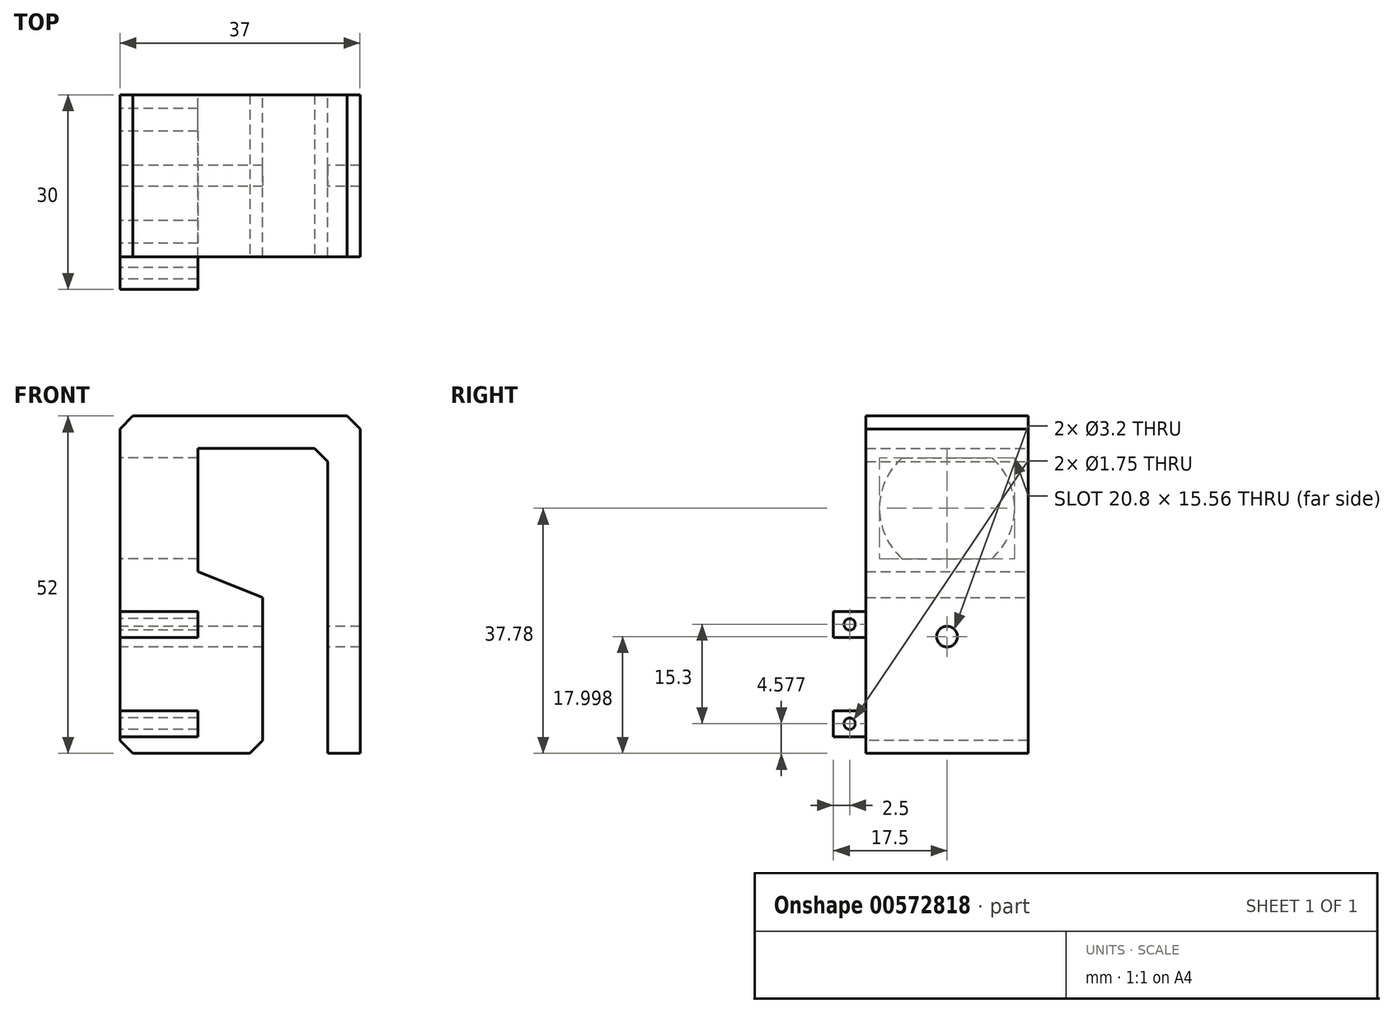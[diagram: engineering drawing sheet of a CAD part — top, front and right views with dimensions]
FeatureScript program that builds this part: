
annotation { "Feature Type Name" : "Feature", "Feature Type Description" : "" }
export const myFeature = defineFeature(function(context is Context, id is Id, definition is map)
    precondition{}
    {
        {
            var Q0;
            Q0=qCreatedBy(makeId("Front.planeOp"),FACE);
            var sketch = newSketch(context, id + "F0", { "sketchPlane" : qUnion([Q0])});
            skLineSegment(sketch, "E0.bottom", {"start": v(-45.23, 26.88) * mm, "end": v(-8.23, 26.88) * mm});
            skLineSegment(sketch, "E0.top", {"start": v(-33.23, 21.88) * mm, "end": v(-13.23, 21.88) * mm});
            skLineSegment(sketch, "E1.top", {"start": v(-8.23, -25.12) * mm, "end": v(-13.23, -25.12) * mm});
            skLineSegment(sketch, "E1.right", {"start": v(-13.23, 21.88) * mm, "end": v(-13.23, -25.12) * mm});
            skLineSegment(sketch, "E2.right", {"start": v(-33.23, 21.88) * mm, "end": v(-33.23, 2.88) * mm});
            skLineSegment(sketch, "E3.bottom", {"start": v(-33.23, 2.88) * mm, "end": v(-23.23, -1.12) * mm});
            skLineSegment(sketch, "E3.right", {"start": v(-23.23, -1.12) * mm, "end": v(-23.23, -25.12) * mm});
            skLineSegment(sketch, "E4", {"start": v(-8.23, 26.88) * mm, "end": v(-8.23, -25.12) * mm});
            skLineSegment(sketch, "E5", {"start": v(-45.23, 26.88) * mm, "end": v(-45.23, -25.12) * mm});
            skLineSegment(sketch, "E6", {"start": v(-45.23, -25.12) * mm, "end": v(-23.23, -25.12) * mm});
            skSolve(sketch);
        }
        {
            var Q0;
            Q0 = qSketchRegion(id + "F0", true);
            extrude(context, id + "F1", {"entities" : qUnion([Q0]), "depth" : 25 * mm, "offsetDistance" : 25 * mm});
        }
        {
            var Q0;
            Q0=makeQuery(id+"F1.opExtrude","SWEPT_FACE",FACE,{"disambiguationData":[OSD([sQuery(id+"F0.wireOp",EDGE,"E5")])]});
            var sketch = newSketch(context, id + "F2", { "sketchPlane" : qUnion([Q0])});
            skArc(sketch, "E7", {"start": v(5.6, 20.44) * mm, "mid": v(2.1, 12.66) * mm, "end": v(5.6, 4.88) * mm});
            skPoint(sketch, "E7.centerSnap0", {"position": v(12.5, 25.39) * mm});
            skLineSegment(sketch, "E8.bottom", {"start": v(19.4, 20.44) * mm, "end": v(5.6, 20.44) * mm});
            skLineSegment(sketch, "E8.top", {"start": v(19.4, 4.88) * mm, "end": v(5.6, 4.88) * mm});
            skArc(sketch, "E9.trimOffspring", {"start": v(19.4, 4.88) * mm, "mid": v(22.9, 12.66) * mm, "end": v(19.4, 20.44) * mm});
            skPoint(sketch, "E10", {"position": v(12.5, 26.88) * mm});
            skSolve(sketch);
        }
        {
            var Q0;
            Q0 = qSketchRegion(id + "F2", true);
            extrude(context, id + "F3", {"entities" : qUnion([Q0]), "operationType" : NewBodyOperationType.REMOVE, "oppositeDirection" : true, "depth" : 25 * mm, "offsetDistance" : 25 * mm});
        }
        {
            var Q0;
            Q0=makeQuery(id+"F1.opExtrude","SWEPT_FACE",FACE,{"disambiguationData":[OSD([sQuery(id+"F0.wireOp",EDGE,"E5")])]});
            var sketch = newSketch(context, id + "F4", { "sketchPlane" : qUnion([Q0])});
            skCircle(sketch, "E11", {"center": v(12.5, -7.12) * mm, "radius": 1.6 * mm});
            skPoint(sketch, "E11.centerSnap0", {"position": v(12.5, 4.88) * mm});
            skSolve(sketch);
        }
        {
            var Q0;
            Q0 = qSketchRegion(id + "F4", true);
            extrude(context, id + "F5", {"entities" : qUnion([Q0]), "operationType" : NewBodyOperationType.REMOVE, "endBound" : BoundingType.THROUGH_ALL, "oppositeDirection" : true, "depth" : 25 * mm, "offsetDistance" : 25 * mm});
        }
        {
            var Q0;
            Q0=makeQuery(id+"F1.opExtrude","SWEPT_EDGE",EDGE,{"disambiguationData":[OSD([sQuery(id+"F0.wireOp",EDGE,"E5"),sQuery(id+"F0.wireOp",EDGE,"E6")])]});
            var Q1;
            Q1=makeQuery(id+"F1.opExtrude","SWEPT_EDGE",EDGE,{"disambiguationData":[OSD([sQuery(id+"F0.wireOp",EDGE,"E3.right"),sQuery(id+"F0.wireOp",EDGE,"E6")])]});
            var Q2;
            Q2=makeQuery(id+"F1.opExtrude","SWEPT_EDGE",EDGE,{"disambiguationData":[OSD([sQuery(id+"F0.wireOp",EDGE,"E0.top"),sQuery(id+"F0.wireOp",EDGE,"E1.right")])]});
            var Q3;
            Q3=makeQuery(id+"F1.opExtrude","SWEPT_EDGE",EDGE,{"disambiguationData":[OSD([sQuery(id+"F0.wireOp",EDGE,"E0.bottom"),sQuery(id+"F0.wireOp",EDGE,"E4")])]});
            var Q4;
            Q4=makeQuery(id+"F1.opExtrude","SWEPT_EDGE",EDGE,{"disambiguationData":[OSD([sQuery(id+"F0.wireOp",EDGE,"E0.bottom"),sQuery(id+"F0.wireOp",EDGE,"E5")])]});
            chamfer(context, id + "F6", {"entities" : qUnion([Q0, Q1, Q2, Q3, Q4]), "width" : 2 * mm, "tangentPropagation" : true});
        }
        {
            var Q0;
            Q0=makeQuery(id+"F1.opExtrude","SWEPT_FACE",FACE,{"disambiguationData":[OSD([sQuery(id+"F0.wireOp",EDGE,"E5")])]});
            var sketch = newSketch(context, id + "F7", { "sketchPlane" : qUnion([Q0])});
            skLineSegment(sketch, "E12.bottom", {"start": v(25, -18.54) * mm, "end": v(30, -18.54) * mm});
            skLineSegment(sketch, "E12.top", {"start": v(25, -22.54) * mm, "end": v(30, -22.54) * mm});
            skLineSegment(sketch, "E12.left", {"start": v(25, -18.54) * mm, "end": v(25, -22.54) * mm});
            skLineSegment(sketch, "E12.right", {"start": v(30, -18.54) * mm, "end": v(30, -22.54) * mm});
            skLineSegment(sketch, "E13.bottom", {"start": v(25, -3.24) * mm, "end": v(30, -3.24) * mm});
            skLineSegment(sketch, "E13.top", {"start": v(25, -7.24) * mm, "end": v(30, -7.24) * mm});
            skLineSegment(sketch, "E13.left", {"start": v(25, -3.24) * mm, "end": v(25, -7.24) * mm});
            skLineSegment(sketch, "E13.right", {"start": v(30, -3.24) * mm, "end": v(30, -7.24) * mm});
            skCircle(sketch, "E14", {"center": v(27.5, -5.24) * mm, "radius": 0.88 * mm});
            skPoint(sketch, "E14.centerSnap0", {"position": v(30, -5.24) * mm});
            skPoint(sketch, "E14.centerSnap1", {"position": v(27.5, -3.24) * mm});
            skCircle(sketch, "E15", {"center": v(27.5, -20.54) * mm, "radius": 0.88 * mm});
            skPoint(sketch, "E15.centerSnap0", {"position": v(27.5, -18.54) * mm});
            skPoint(sketch, "E15.centerSnap1", {"position": v(30, -20.54) * mm});
            skSolve(sketch);
        }
        {
            var Q0;
            Q0 = qSketchRegion(id + "F7", true);
            var Q1;
            Q1=makeQuery(id+"F1.opExtrude","SWEPT_FACE",FACE,{"disambiguationData":[OSD([sQuery(id+"F0.wireOp",EDGE,"E2.right")])]});
            extrude(context, id + "F8", {"entities" : qUnion([Q0]), "operationType" : NewBodyOperationType.ADD, "endBound" : BoundingType.UP_TO_SURFACE, "oppositeDirection" : true, "depth" : 25 * mm, "endBoundEntityFace" : qUnion([Q1]), "offsetDistance" : 25 * mm});
        }
    });
